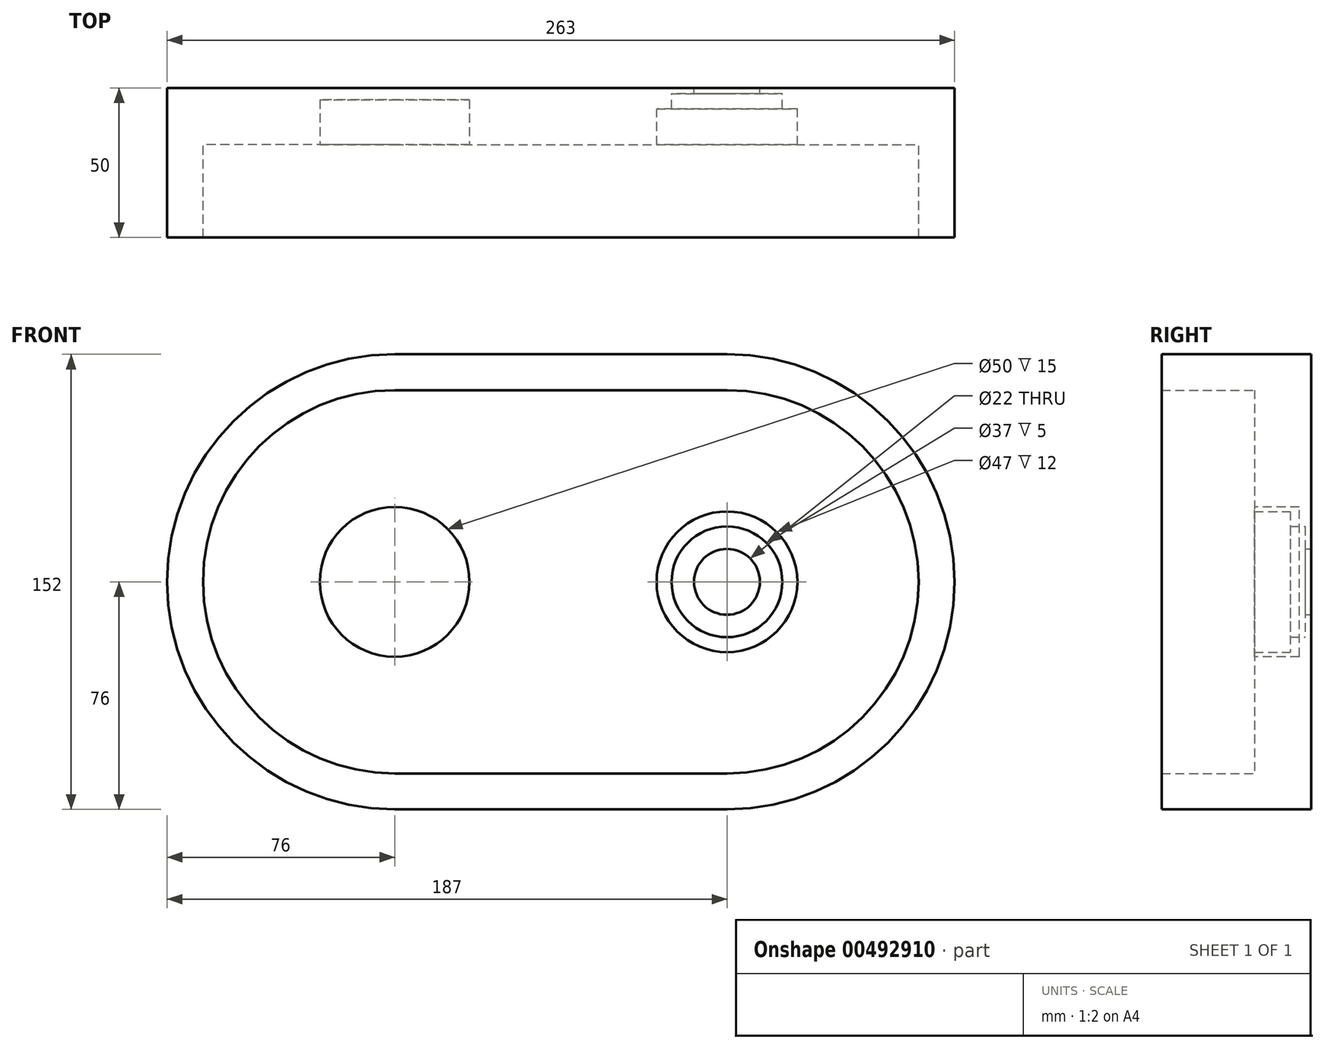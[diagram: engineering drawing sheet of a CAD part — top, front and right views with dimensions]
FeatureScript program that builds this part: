
annotation { "Feature Type Name" : "Feature", "Feature Type Description" : "" }
export const myFeature = defineFeature(function(context is Context, id is Id, definition is map)
    precondition{}
    {
        {
            var Q0;
            Q0=qCreatedBy(makeId("Front.planeOp"),FACE);
            var sketch = newSketch(context, id + "F0", { "sketchPlane" : qUnion([Q0])});
            skArc(sketch, "E0", {"start": v(-111, 76) * mm, "mid": v(-187, 0) * mm, "end": v(-111, -76) * mm});
            skArc(sketch, "E1", {"start": v(0, -76) * mm, "mid": v(76, 0) * mm, "end": v(0, 76) * mm});
            skLineSegment(sketch, "E2", {"start": v(-111, 76) * mm, "end": v(0, 76) * mm});
            skLineSegment(sketch, "E3", {"start": v(-111, -76) * mm, "end": v(0, -76) * mm});
            skSolve(sketch);
        }
        {
            var Q0;
            Q0=qCreatedBy(makeId("Front.planeOp"),FACE);
            cPlane(context, id + "F1", {"entities" : qUnion([Q0]), "cplaneType" : CPlaneType.OFFSET, "offset" : 19 * mm, "width" : 150 * mm, "height" : 150 * mm});
        }
        {
            var Q0;
            Q0=qCreatedBy(id+"F1.planeOp",FACE);
            var sketch = newSketch(context, id + "F2", { "sketchPlane" : qUnion([Q0])});
            skArc(sketch, "E4", {"start": v(-111, 64) * mm, "mid": v(-175, 0) * mm, "end": v(-111, -64) * mm});
            skArc(sketch, "E5", {"start": v(0, -64) * mm, "mid": v(64, 0) * mm, "end": v(0, 64) * mm});
            skLineSegment(sketch, "E6", {"start": v(-111, 64) * mm, "end": v(0, 64) * mm});
            skLineSegment(sketch, "E7", {"start": v(-111, -64) * mm, "end": v(0, -64) * mm});
            skCircle(sketch, "E8", {"center": v(-111, 0) * mm, "radius": 25 * mm});
            skSolve(sketch);
        }
        {
            var Q0;
            Q0=makeQuery(id+"F0.imprint","IMPRINT",FACE,{"disambiguationData":[TD([[makeQuery(id+"F0.imprint","IMPRINT",EDGE,{"derivedFrom":sQuery(id+"F0.wireOp",EDGE,"E0")}),1.0]])]});
            extrude(context, id + "F3", {"entities" : qUnion([Q0]), "depth" : 50 * mm, "offsetDistance" : 25 * mm});
        }
        {
            var Q0;
            Q0=makeQuery(id+"F2.imprint","IMPRINT",FACE,{"disambiguationData":[TD([[makeQuery(id+"F2.imprint","IMPRINT",EDGE,{"derivedFrom":sQuery(id+"F2.wireOp",EDGE,"E8")}),1.0]])]});
            extrude(context, id + "F4", {"entities" : qUnion([Q0]), "operationType" : NewBodyOperationType.REMOVE, "oppositeDirection" : true, "depth" : 15 * mm, "offsetDistance" : 25 * mm});
        }
        {
            var Q0;
            Q0=makeQuery(id+"F2.imprint","IMPRINT",FACE,{"disambiguationData":[TD([[makeQuery(id+"F2.imprint","IMPRINT",EDGE,{"derivedFrom":sQuery(id+"F2.wireOp",EDGE,"E8")}),1.0]])]});
            extrude(context, id + "F5", {"entities" : qUnion([Q0]), "operationType" : NewBodyOperationType.REMOVE, "depth" : 35 * mm, "offsetDistance" : 25 * mm});
        }
        {
            var Q0;
            Q0=makeQuery(id+"F2.imprint","IMPRINT",FACE,{"disambiguationData":[TD([[makeQuery(id+"F2.imprint","IMPRINT",EDGE,{"derivedFrom":sQuery(id+"F2.wireOp",EDGE,"E4")}),1.0]])]});
            extrude(context, id + "F6", {"entities" : qUnion([Q0]), "operationType" : NewBodyOperationType.REMOVE, "depth" : 35 * mm, "offsetDistance" : 25 * mm});
        }
        {
            var Q0;
            Q0=qCreatedBy(makeId("Right.planeOp"),FACE);
            var sketch = newSketch(context, id + "F7", { "sketchPlane" : qUnion([Q0])});
            skLineSegment(sketch, "E9", {"start": v(-67.07, 0) * mm, "end": v(13.94, 0) * mm, "construction": true});
            skLineSegment(sketch, "E10", {"start": v(-2, 11) * mm, "end": v(0, 11) * mm});
            skLineSegment(sketch, "E11", {"start": v(-7, 18.5) * mm, "end": v(-2, 18.5) * mm});
            skLineSegment(sketch, "E12", {"start": v(-2, 11) * mm, "end": v(-2, 18.5) * mm});
            skLineSegment(sketch, "E13", {"start": v(-7, 18.5) * mm, "end": v(-7, 23.5) * mm});
            skLineSegment(sketch, "E14", {"start": v(-19, 23.5) * mm, "end": v(-19, 0) * mm});
            skLineSegment(sketch, "E15", {"start": v(-19, 0) * mm, "end": v(0, 0) * mm});
            skLineSegment(sketch, "E16", {"start": v(0, 0) * mm, "end": v(0, 11) * mm});
            skLineSegment(sketch, "E17", {"start": v(-19, 23.5) * mm, "end": v(-7, 23.5) * mm});
            skSolve(sketch);
        }
        {
            var Q0;
            Q0 = qSketchRegion(id + "F7", true);
            var Q1;
            Q1=makeQuery(id+"F3.opExtrude","SWEPT_FACE",FACE,{"disambiguationData":[OSD([sQuery(id+"F0.wireOp",EDGE,"E1")])]});
            revolve(context, id + "F8", {"operationType" : NewBodyOperationType.REMOVE, "entities" : qUnion([Q0]), "axis" : qUnion([Q1]), "revolveType" : RevolveType.ONE_DIRECTION, "oppositeDirection" : true, "angle" : 360 * degree});
        }
    });
